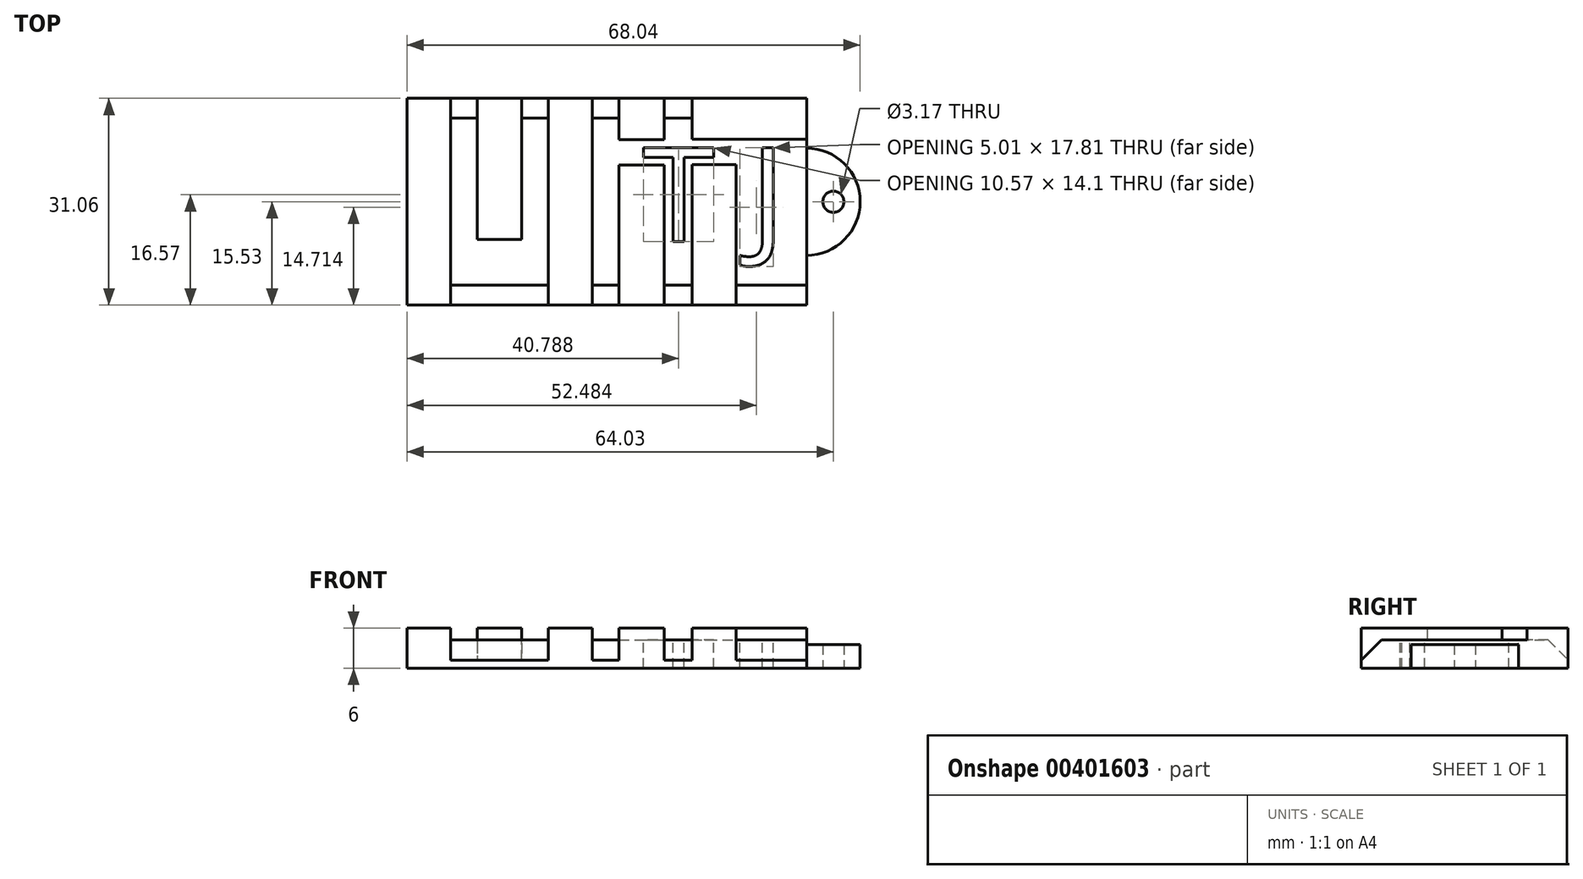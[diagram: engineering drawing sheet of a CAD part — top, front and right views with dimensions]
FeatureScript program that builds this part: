
annotation { "Feature Type Name" : "Feature", "Feature Type Description" : "" }
export const myFeature = defineFeature(function(context is Context, id is Id, definition is map)
    precondition{}
    {
        {
            var Q0;
            Q0=qCreatedBy(makeId("Top.planeOp"),FACE);
            var sketch = newSketch(context, id + "F0", { "sketchPlane" : qUnion([Q0])});
            skLineSegment(sketch, "E0.bottom", {"start": v(-74.33, -7.04) * mm, "end": v(-67.75, -7.04) * mm});
            skLineSegment(sketch, "E0.top", {"start": v(-74.33, -38.1) * mm, "end": v(-67.75, -38.1) * mm});
            skLineSegment(sketch, "E0.left", {"start": v(-74.33, -7.04) * mm, "end": v(-74.33, -38.1) * mm});
            skLineSegment(sketch, "E0.right", {"start": v(-14.33, -7.04) * mm, "end": v(-14.33, -13.21) * mm});
            skLineSegment(sketch, "E1", {"start": v(-67.75, -7.04) * mm, "end": v(-67.75, -38.1) * mm});
            skLineSegment(sketch, "E2", {"start": v(-63.76, -7.04) * mm, "end": v(-63.76, -28.21) * mm});
            skLineSegment(sketch, "E3", {"start": v(-63.76, -28.21) * mm, "end": v(-57.1, -28.21) * mm});
            skLineSegment(sketch, "E4", {"start": v(-57.1, -28.21) * mm, "end": v(-57.1, -7.04) * mm});
            skLineSegment(sketch, "E5", {"start": v(-53.1, -7.04) * mm, "end": v(-53.1, -38.1) * mm});
            skLineSegment(sketch, "E6", {"start": v(-46.52, -38.1) * mm, "end": v(-46.52, -7.04) * mm});
            skLineSegment(sketch, "E7", {"start": v(-42.48, -7.04) * mm, "end": v(-42.48, -13.24) * mm});
            skLineSegment(sketch, "E8", {"start": v(-42.48, -13.24) * mm, "end": v(-35.72, -13.24) * mm});
            skLineSegment(sketch, "E9", {"start": v(-35.72, -13.24) * mm, "end": v(-35.72, -7.04) * mm});
            skLineSegment(sketch, "E10", {"start": v(-42.48, -38.1) * mm, "end": v(-42.48, -17.05) * mm});
            skLineSegment(sketch, "E11", {"start": v(-42.48, -17.05) * mm, "end": v(-35.72, -17.05) * mm});
            skLineSegment(sketch, "E12", {"start": v(-35.72, -17.05) * mm, "end": v(-35.72, -38.1) * mm});
            skLineSegment(sketch, "E13", {"start": v(-24.92, -17) * mm, "end": v(-24.92, -38.1) * mm});
            skLineSegment(sketch, "E14", {"start": v(-31.54, -7.04) * mm, "end": v(-31.54, -13.21) * mm});
            skLineSegment(sketch, "E15", {"start": v(-31.54, -13.21) * mm, "end": v(-14.33, -13.21) * mm});
            skLineSegment(sketch, "E16", {"start": v(-31.54, -38.1) * mm, "end": v(-31.54, -17) * mm});
            skPoint(sketch, "E16.startSnap0", {"position": v(-31.54, -10.13) * mm});
            skLineSegment(sketch, "E17", {"start": v(-31.54, -17) * mm, "end": v(-24.92, -17) * mm});
            skCircle(sketch, "E18", {"center": v(-10.3, -22.57) * mm, "radius": 1.59 * mm});
            skArc(sketch, "E19", {"start": v(-14.33, -30.62) * mm, "mid": v(-6.29, -22.57) * mm, "end": v(-14.33, -14.52) * mm});
            skLineSegment(sketch, "E20.trimOffspring", {"start": v(-63.76, -7.04) * mm, "end": v(-57.1, -7.04) * mm});
            skLineSegment(sketch, "E21.trimOffspring", {"start": v(-53.1, -7.04) * mm, "end": v(-46.52, -7.04) * mm});
            skLineSegment(sketch, "E22.trimOffspring", {"start": v(-42.48, -7.04) * mm, "end": v(-35.72, -7.04) * mm});
            skLineSegment(sketch, "E23.trimOffspring", {"start": v(-31.54, -7.04) * mm, "end": v(-14.33, -7.04) * mm});
            skLineSegment(sketch, "E24.trimOffspring", {"start": v(-31.54, -38.1) * mm, "end": v(-24.92, -38.1) * mm});
            skLineSegment(sketch, "E25.trimOffspring", {"start": v(-42.48, -38.1) * mm, "end": v(-35.72, -38.1) * mm});
            skLineSegment(sketch, "E26.trimOffspring", {"start": v(-53.1, -38.1) * mm, "end": v(-46.52, -38.1) * mm});
            skLineSegment(sketch, "E27.trimOffspring", {"start": v(-14.33, -14.52) * mm, "end": v(-14.33, -30.62) * mm});
            skPoint(sketch, "E28.orphan", {"position": v(-14.33, -38.1) * mm});
            skLineSegment(sketch, "E29", {"start": v(-74.33, -7.04) * mm, "end": v(-14.33, -7.04) * mm});
            skLineSegment(sketch, "E30", {"start": v(-74.33, -38.1) * mm, "end": v(-14.33, -38.1) * mm});
            skLineSegment(sketch, "E31", {"start": v(-14.33, -13.21) * mm, "end": v(-14.33, -38.1) * mm});
            skSolve(sketch);
        }
        {
            var Q0;
            {var subQ2=sQuery(id+"F0.wireOp",EDGE,"E1");Q0=makeQuery(id+"F0.imprint","IMPRINT",FACE,{"disambiguationData":[TD([[makeQuery(id+"F0.imprint","IMPRINT",EDGE,{"derivedFrom":subQ2}),1.0]])]});}
            var Q1;
            {var subQ12=sQuery(id+"F0.wireOp",EDGE,"E6");Q1=makeQuery(id+"F0.imprint","IMPRINT",FACE,{"disambiguationData":[TD([[makeQuery(id+"F0.imprint","IMPRINT",EDGE,{"derivedFrom":subQ12}),-1.0]])]});}
            extrude(context, id + "F1", {"entities" : qUnion([Q0, Q1]), "depth" : 4.2 * mm, "offsetDistance" : 25 * mm});
        }
        {
            var Q0;
            {var subQ0=sQuery(id+"F0.wireOp",EDGE,"E0.left");Q0=makeQuery(id+"F0.imprint","IMPRINT",FACE,{"disambiguationData":[TD([[makeQuery(id+"F0.imprint","IMPRINT",EDGE,{"derivedFrom":subQ0}),1.0]])]});}
            var Q1;
            {var subQ0=sQuery(id+"F0.wireOp",EDGE,"E2");Q1=makeQuery(id+"F0.imprint","IMPRINT",FACE,{"disambiguationData":[TD([[makeQuery(id+"F0.imprint","IMPRINT",EDGE,{"derivedFrom":subQ0}),1.0]])]});}
            var Q2;
            {var subQ0=sQuery(id+"F0.wireOp",EDGE,"E5");Q2=makeQuery(id+"F0.imprint","IMPRINT",FACE,{"disambiguationData":[TD([[makeQuery(id+"F0.imprint","IMPRINT",EDGE,{"derivedFrom":subQ0}),1.0]])]});}
            var Q3;
            {var subQ0=sQuery(id+"F0.wireOp",EDGE,"E7");Q3=makeQuery(id+"F0.imprint","IMPRINT",FACE,{"disambiguationData":[TD([[makeQuery(id+"F0.imprint","IMPRINT",EDGE,{"derivedFrom":subQ0}),1.0]])]});}
            var Q4;
            {var subQ0=sQuery(id+"F0.wireOp",EDGE,"E10");Q4=makeQuery(id+"F0.imprint","IMPRINT",FACE,{"disambiguationData":[TD([[makeQuery(id+"F0.imprint","IMPRINT",EDGE,{"derivedFrom":subQ0}),-1.0]])]});}
            var Q5;
            {var subQ0=sQuery(id+"F0.wireOp",EDGE,"E13");Q5=makeQuery(id+"F0.imprint","IMPRINT",FACE,{"disambiguationData":[TD([[makeQuery(id+"F0.imprint","IMPRINT",EDGE,{"derivedFrom":subQ0}),-1.0]])]});}
            var Q6;
            {var subQ0=sQuery(id+"F0.wireOp",EDGE,"E0.right");Q6=makeQuery(id+"F0.imprint","IMPRINT",FACE,{"disambiguationData":[TD([[makeQuery(id+"F0.imprint","IMPRINT",EDGE,{"derivedFrom":subQ0}),-1.0]])]});}
            extrude(context, id + "F2", {"entities" : qUnion([Q0, Q1, Q2, Q3, Q4, Q5, Q6]), "operationType" : NewBodyOperationType.ADD, "depth" : 6 * mm, "offsetDistance" : 25 * mm});
        }
        {
            var Q0;
            Q0=makeQuery(id+"F0.imprint","IMPRINT",FACE,{"disambiguationData":[TD([[makeQuery(id+"F0.imprint","IMPRINT",EDGE,{"derivedFrom":sQuery(id+"F0.wireOp",EDGE,"E18")}),-1.0]])]});
            extrude(context, id + "F3", {"entities" : qUnion([Q0]), "operationType" : NewBodyOperationType.ADD, "depth" : 3.5 * mm, "offsetDistance" : 25 * mm});
        }
        {
            var Q0;
            Q0=makeQuery(id+"F1.opExtrude","CAP_FACE",FACE,{"disambiguationData":[OSD([sQuery(id+"F0.wireOp",EDGE,"E6"),sQuery(id+"F0.wireOp",EDGE,"E7"),sQuery(id+"F0.wireOp",EDGE,"E8"),sQuery(id+"F0.wireOp",EDGE,"E9"),sQuery(id+"F0.wireOp",EDGE,"E10"),sQuery(id+"F0.wireOp",EDGE,"E11"),sQuery(id+"F0.wireOp",EDGE,"E12"),sQuery(id+"F0.wireOp",EDGE,"E13"),sQuery(id+"F0.wireOp",EDGE,"E14"),sQuery(id+"F0.wireOp",EDGE,"E15"),sQuery(id+"F0.wireOp",EDGE,"E16"),sQuery(id+"F0.wireOp",EDGE,"E17"),sQuery(id+"F0.wireOp",EDGE,"E29"),sQuery(id+"F0.wireOp",EDGE,"E30"),sQuery(id+"F0.wireOp",EDGE,"E31")])],"isStart":false});
            var sketch = newSketch(context, id + "F4", { "sketchPlane" : qUnion([Q0])});
            skPoint(sketch, "E32.endSnap0", {"position": v(-28.23, -15.1) * mm});
            skPoint(sketch, "E33.start.orphan", {"position": v(-39.1, -13.24) * mm});
            skPoint(sketch, "E34.orphan", {"position": v(-28.23, -13.21) * mm});
            skPoint(sketch, "E35.orphan", {"position": v(-28.23, -17) * mm});
            skPoint(sketch, "E36.start.orphan", {"position": v(-39.1, -17.05) * mm});
            skText(sketch, "E37", { "text": "J", "fontName": "OpenSans-Regular.ttf"});
            skText(sketch, "E38", { "text": "T", "fontName": "OpenSans-Regular.ttf"});
            const initialGuessF4  = {"E37": [-0.02281, -0.02858, 1, 0, 0.01422], "E38": [-0.039, -0.02858, 1, 0, 0.01422]};
            skSetInitialGuess(sketch, initialGuessF4);
            skSolve(sketch);
        }
        {
            var Q0;
            Q0=makeQuery(id+"F4.imprint","IMPRINT",FACE,{"disambiguationData":[TD([[makeQuery(id+"F4.imprint","IMPRINT",EDGE,{"derivedFrom":sQuery(id+"F4.wireOp",EDGE,"E38.sketch_text.stroke-0")}),-1.0]])]});
            var Q1;
            Q1=makeQuery(id+"F4.imprint","IMPRINT",FACE,{"disambiguationData":[TD([[makeQuery(id+"F4.imprint","IMPRINT",EDGE,{"derivedFrom":sQuery(id+"F4.wireOp",EDGE,"E37.sketch_text.stroke-0")}),-1.0]])]});
            extrude(context, id + "F5", {"entities" : qUnion([Q0, Q1]), "operationType" : NewBodyOperationType.REMOVE, "oppositeDirection" : true, "depth" : 25 * mm, "offsetDistance" : 25 * mm});
        }
        {
            var Q0;
            {var subQ0=sQuery(id+"F0.wireOp",EDGE,"E29");Q0=makeQuery(id+"F1.opExtrude","CAP_EDGE",EDGE,{"disambiguationData":[OSD([subQ0]),TDD([makeQuery(id+"F0.imprint","IMPRINT",EDGE,{"disambiguationData":[TD([[makeQuery(id+"F0.imprint","INTERSECT",VERTEX,{"derivedFrom":[sQuery(id+"F0.wireOp",EDGE,"E1"),subQ0]}),-1.0]])],"derivedFrom":subQ0})])],"isStart":false});}
            var Q1;
            {var subQ0=sQuery(id+"F0.wireOp",EDGE,"E29");Q1=makeQuery(id+"F1.opExtrude","CAP_EDGE",EDGE,{"disambiguationData":[OSD([subQ0]),TDD([makeQuery(id+"F0.imprint","IMPRINT",EDGE,{"disambiguationData":[TD([[makeQuery(id+"F0.imprint","INTERSECT",VERTEX,{"derivedFrom":[sQuery(id+"F0.wireOp",EDGE,"E4"),subQ0]}),-1.0]])],"derivedFrom":subQ0})])],"isStart":false});}
            var Q2;
            {var subQ0=sQuery(id+"F0.wireOp",EDGE,"E29");Q2=makeQuery(id+"F1.opExtrude","CAP_EDGE",EDGE,{"disambiguationData":[OSD([subQ0]),TDD([makeQuery(id+"F0.imprint","IMPRINT",EDGE,{"disambiguationData":[TD([[makeQuery(id+"F0.imprint","INTERSECT",VERTEX,{"derivedFrom":[sQuery(id+"F0.wireOp",EDGE,"E6"),subQ0]}),-1.0]])],"derivedFrom":subQ0})])],"isStart":false});}
            var Q3;
            {var subQ0=sQuery(id+"F0.wireOp",EDGE,"E29");Q3=makeQuery(id+"F1.opExtrude","CAP_EDGE",EDGE,{"disambiguationData":[OSD([subQ0]),TDD([makeQuery(id+"F0.imprint","IMPRINT",EDGE,{"disambiguationData":[TD([[makeQuery(id+"F0.imprint","INTERSECT",VERTEX,{"derivedFrom":[sQuery(id+"F0.wireOp",EDGE,"E9"),subQ0]}),-1.0]])],"derivedFrom":subQ0})])],"isStart":false});}
            var Q4;
            {var subQ0=sQuery(id+"F0.wireOp",EDGE,"E30");Q4=makeQuery(id+"F1.opExtrude","CAP_EDGE",EDGE,{"disambiguationData":[OSD([subQ0]),TDD([makeQuery(id+"F0.imprint","IMPRINT",EDGE,{"disambiguationData":[TD([[makeQuery(id+"F0.imprint","INTERSECT",VERTEX,{"derivedFrom":[sQuery(id+"F0.wireOp",EDGE,"E1"),subQ0]}),-1.0]])],"derivedFrom":subQ0})])],"isStart":false});}
            var Q5;
            {var subQ0=sQuery(id+"F0.wireOp",EDGE,"E30");Q5=makeQuery(id+"F1.opExtrude","CAP_EDGE",EDGE,{"disambiguationData":[OSD([subQ0]),TDD([makeQuery(id+"F0.imprint","IMPRINT",EDGE,{"disambiguationData":[TD([[makeQuery(id+"F0.imprint","INTERSECT",VERTEX,{"derivedFrom":[sQuery(id+"F0.wireOp",EDGE,"E6"),subQ0]}),-1.0]])],"derivedFrom":subQ0})])],"isStart":false});}
            var Q6;
            {var subQ0=sQuery(id+"F0.wireOp",EDGE,"E30");Q6=makeQuery(id+"F1.opExtrude","CAP_EDGE",EDGE,{"disambiguationData":[OSD([subQ0]),TDD([makeQuery(id+"F0.imprint","IMPRINT",EDGE,{"disambiguationData":[TD([[makeQuery(id+"F0.imprint","INTERSECT",VERTEX,{"derivedFrom":[sQuery(id+"F0.wireOp",EDGE,"E12"),subQ0]}),-1.0]])],"derivedFrom":subQ0})])],"isStart":false});}
            var Q7;
            {var subQ0=sQuery(id+"F0.wireOp",EDGE,"E30");Q7=makeQuery(id+"F1.opExtrude","CAP_EDGE",EDGE,{"disambiguationData":[OSD([subQ0]),TDD([makeQuery(id+"F0.imprint","IMPRINT",EDGE,{"disambiguationData":[TD([[makeQuery(id+"F0.imprint","INTERSECT",VERTEX,{"derivedFrom":[sQuery(id+"F0.wireOp",EDGE,"E13"),subQ0]}),-1.0]])],"derivedFrom":subQ0})])],"isStart":false});}
            chamfer(context, id + "F6", {"entities" : qUnion([Q0, Q1, Q2, Q3, Q4, Q5, Q6, Q7]), "width" : 3 * mm, "tangentPropagation" : true});
        }
    });
